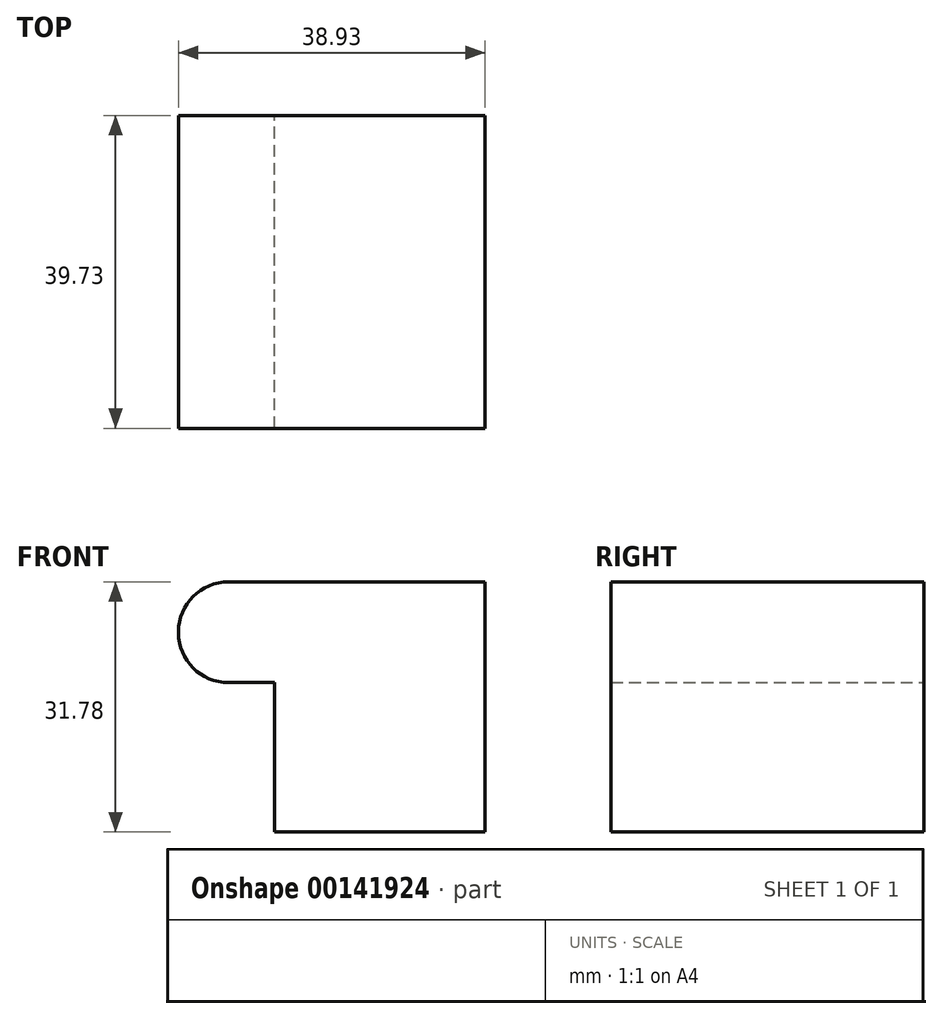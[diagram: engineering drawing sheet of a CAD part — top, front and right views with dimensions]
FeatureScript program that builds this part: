
annotation { "Feature Type Name" : "Feature", "Feature Type Description" : "" }
export const myFeature = defineFeature(function(context is Context, id is Id, definition is map)
    precondition{}
    {
        {
            var Q0;
            Q0=qCreatedBy(makeId("Front.planeOp"),FACE);
            var sketch = newSketch(context, id + "F0", { "sketchPlane" : qUnion([Q0])});
            skLineSegment(sketch, "E0", {"start": v(-46.61, 37.54) * mm, "end": v(-46.61, 37.43) * mm});
            skLineSegment(sketch, "E1", {"start": v(-40.26, 31.08) * mm, "end": v(-34.4, 31.08) * mm});
            skLineSegment(sketch, "E2", {"start": v(-34.4, 31.08) * mm, "end": v(-34.4, 12.11) * mm});
            skLineSegment(sketch, "E3", {"start": v(-34.4, 12.11) * mm, "end": v(-7.68, 12.11) * mm});
            skLineSegment(sketch, "E4", {"start": v(-7.68, 12.11) * mm, "end": v(-7.68, 31.08) * mm});
            skLineSegment(sketch, "E5", {"start": v(-7.68, 43.89) * mm, "end": v(-40.26, 43.89) * mm});
            skPoint(sketch, "E6.orphan", {"position": v(-30.58, 31.08) * mm});
            skPoint(sketch, "E7.visualSharp", {"position": v(-46.61, 43.89) * mm});
            skArc(sketch, "E7.filletArc", {"start": v(-40.26, 43.89) * mm, "mid": v(-44.75, 42.03) * mm, "end": v(-46.61, 37.54) * mm});
            skPoint(sketch, "E8.visualSharp", {"position": v(-4.76, 43.89) * mm});
            skPoint(sketch, "E9.visualSharp", {"position": v(-46.61, 31.08) * mm});
            skArc(sketch, "E9.filletArc", {"start": v(-46.61, 37.43) * mm, "mid": v(-44.75, 32.94) * mm, "end": v(-40.26, 31.08) * mm});
            skLineSegment(sketch, "E10", {"start": v(-7.68, 31.08) * mm, "end": v(-7.68, 43.89) * mm});
            skSolve(sketch);
        }
        {
            var Q0;
            Q0=makeQuery(id+"F0.imprint","IMPRINT",FACE,{"disambiguationData":[TD([[makeQuery(id+"F0.imprint","IMPRINT",EDGE,{"derivedFrom":sQuery(id+"F0.wireOp",EDGE,"E0")}),1.0]])]});
            extrude(context, id + "F1", {"entities" : qUnion([Q0]), "depth" : 39.73 * mm});
        }
    });
